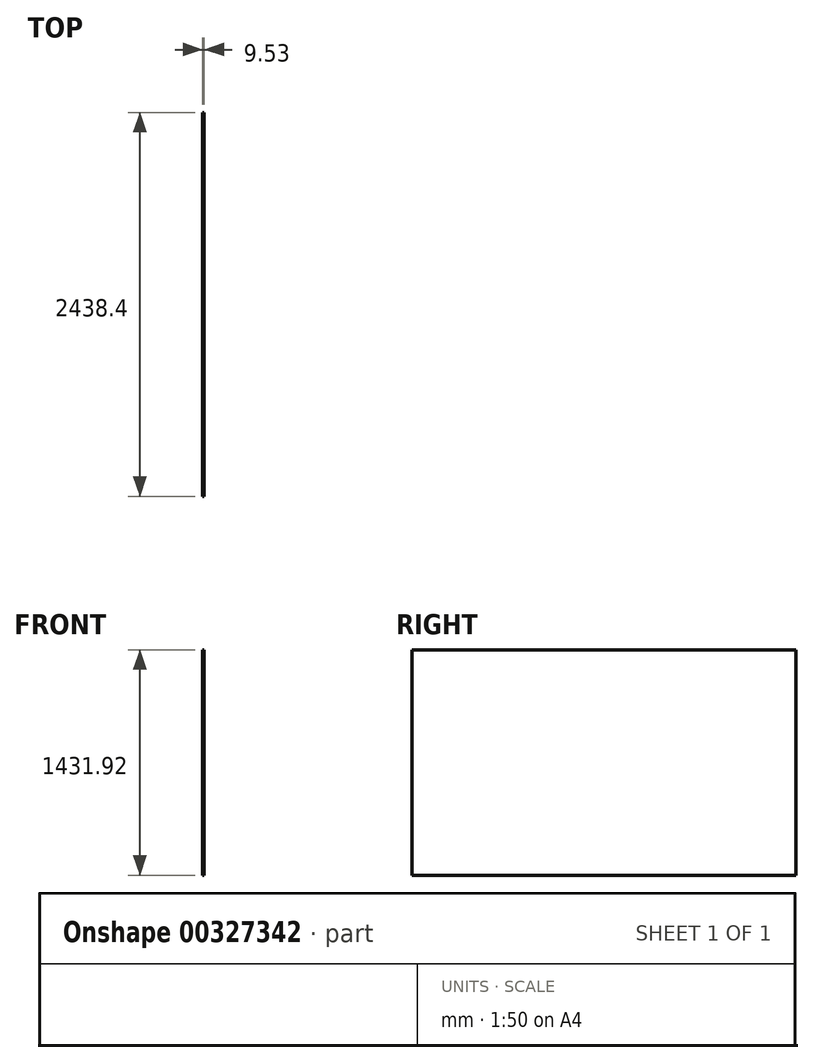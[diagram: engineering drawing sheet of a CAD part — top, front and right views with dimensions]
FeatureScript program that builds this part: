
annotation { "Feature Type Name" : "Feature", "Feature Type Description" : "" }
export const myFeature = defineFeature(function(context is Context, id is Id, definition is map)
    precondition{}
    {
        {
            var Q0;
            Q0=qCreatedBy(makeId("Right.planeOp"),FACE);
            var sketch = newSketch(context, id + "F0", { "sketchPlane" : qUnion([Q0])});
            skLineSegment(sketch, "E0.bottom", {"start": v(-1286.08, 384.41) * mm, "end": v(1152.32, 384.41) * mm});
            skLineSegment(sketch, "E0.top", {"start": v(-1286.08, -1047.51) * mm, "end": v(1152.32, -1047.51) * mm});
            skLineSegment(sketch, "E0.left", {"start": v(-1286.08, 384.41) * mm, "end": v(-1286.08, -1047.51) * mm});
            skLineSegment(sketch, "E0.right", {"start": v(1152.32, 384.41) * mm, "end": v(1152.32, -1047.51) * mm});
            skSolve(sketch);
        }
        {
            var Q0;
            Q0=makeQuery(id+"F0.imprint","IMPRINT",FACE,{"disambiguationData":[TD([[makeQuery(id+"F0.imprint","IMPRINT",EDGE,{"derivedFrom":sQuery(id+"F0.wireOp",EDGE,"E0.bottom")}),-1.0]])]});
            extrude(context, id + "F1", {"entities" : qUnion([Q0]), "depth" : 9.52 * mm});
        }
    });
